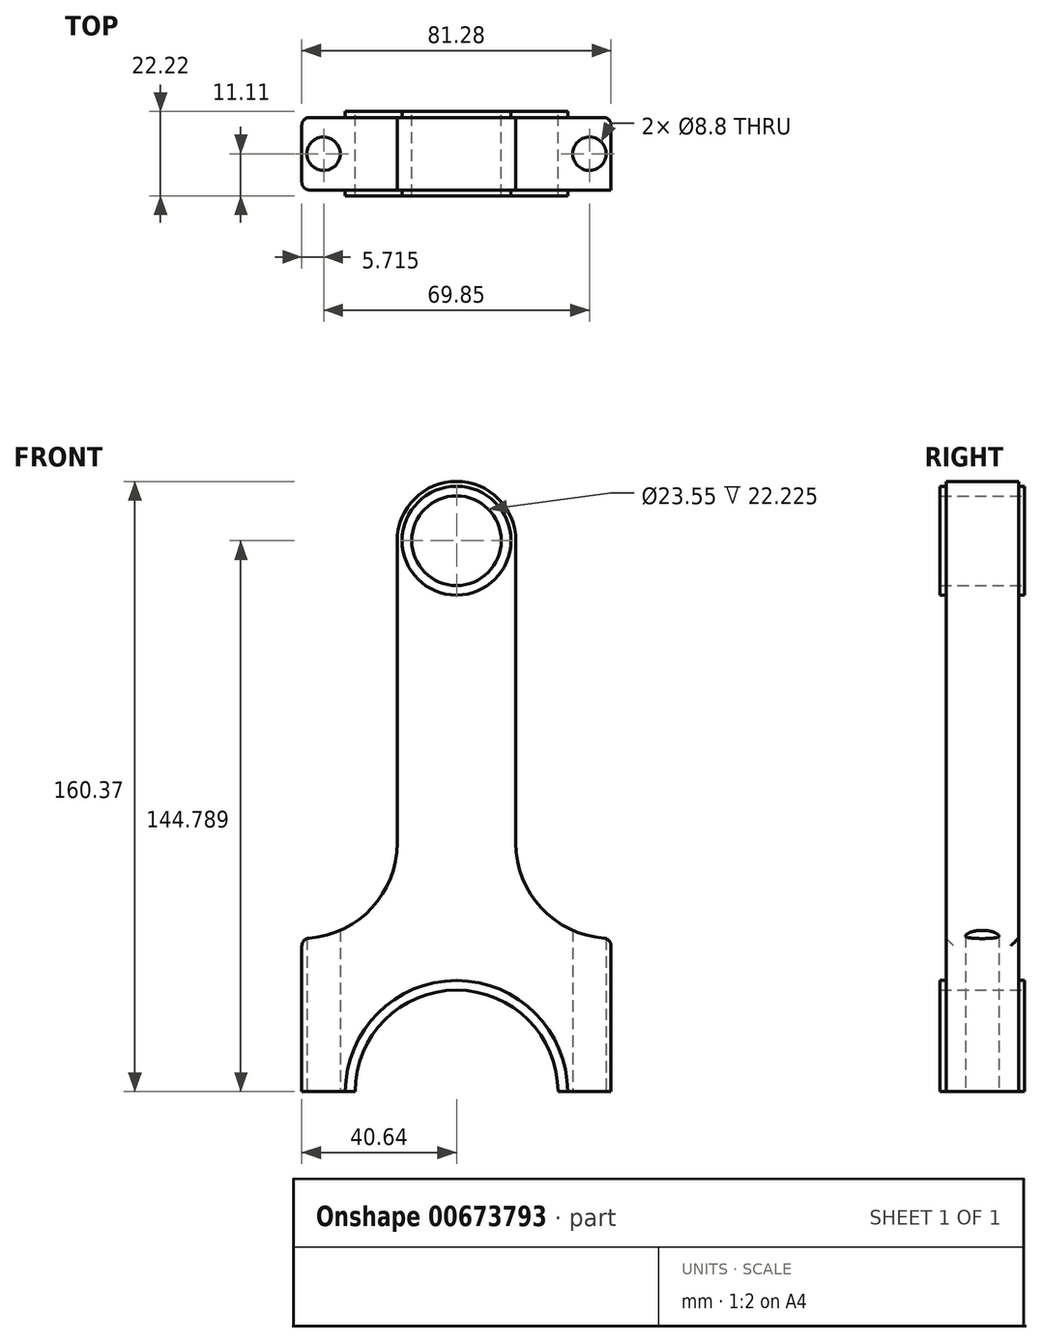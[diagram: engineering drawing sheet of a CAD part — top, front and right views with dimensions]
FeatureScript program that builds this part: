
annotation { "Feature Type Name" : "Feature", "Feature Type Description" : "" }
export const myFeature = defineFeature(function(context is Context, id is Id, definition is map)
    precondition{}
    {
        {
            var Q0;
            Q0=qCreatedBy(makeId("Front.planeOp"),FACE);
            var sketch = newSketch(context, id + "F0", { "sketchPlane" : qUnion([Q0])});
            skCircle(sketch, "E0", {"center": v(0, 0) * mm, "radius": 26.67 * mm});
            skLineSegment(sketch, "E1", {"start": v(26.67, 0) * mm, "end": v(40.64, 0) * mm});
            skLineSegment(sketch, "E2", {"start": v(40.64, 0) * mm, "end": v(40.64, 40.26) * mm});
            skArc(sketch, "E3", {"start": v(15.58, 65.32) * mm, "mid": v(22.92, 47.6) * mm, "end": v(40.64, 40.26) * mm});
            skLineSegment(sketch, "E4", {"start": v(15.58, 65.32) * mm, "end": v(15.58, 144.79) * mm});
            skLineSegment(sketch, "E5", {"start": v(40.64, 40.26) * mm, "end": v(98.37, 40.26) * mm, "construction": true});
            skCircle(sketch, "E6", {"center": v(0, 144.79) * mm, "radius": 11.77 * mm});
            skCircle(sketch, "E7", {"center": v(0, 144.79) * mm, "radius": 15.58 * mm});
            skCircle(sketch, "E8", {"center": v(0, 144.79) * mm, "radius": 14.31 * mm});
            skLineSegment(sketch, "E9.MirrorCS", {"start": v(-15.58, 65.32) * mm, "end": v(-15.58, 144.79) * mm});
            skArc(sketch, "E10.MirrorCS", {"start": v(-15.58, 65.32) * mm, "mid": v(-22.92, 47.6) * mm, "end": v(-40.64, 40.26) * mm});
            skLineSegment(sketch, "E11.MirrorCS", {"start": v(-40.64, 0) * mm, "end": v(-40.64, 40.26) * mm});
            skLineSegment(sketch, "E12.MirrorCS", {"start": v(-26.67, 0) * mm, "end": v(-40.64, 0) * mm});
            skCircle(sketch, "E13", {"center": v(0, 0) * mm, "radius": 29.21 * mm});
            skSolve(sketch);
        }
        {
            var Q0;
            {var subQ6=sQuery(id+"F0.wireOp",EDGE,"E2");Q0=makeQuery(id+"F0.imprint","IMPRINT",FACE,{"disambiguationData":[TD([[makeQuery(id+"F0.imprint","IMPRINT",EDGE,{"derivedFrom":subQ6}),1.0]])]});}
            var Q1;
            Q1=makeQuery(id+"F0.imprint","IMPRINT",FACE,{"disambiguationData":[TD([[makeQuery(id+"F0.imprint","IMPRINT",EDGE,{"derivedFrom":sQuery(id+"F0.wireOp",EDGE,"E8")}),-1.0]])]});
            extrude(context, id + "F1", {"entities" : qUnion([Q0, Q1]), "depth" : 19.05 * mm, "offsetDistance" : 25 * mm, "symmetric" : true});
        }
        {
            var Q0;
            {var subQ0=sQuery(id+"F0.wireOp",EDGE,"E1");var subQ1=sQuery(id+"F0.wireOp",EDGE,"E0");var subQ2=makeQuery(id+"F0.imprint","INTERSECT",VERTEX,{"derivedFrom":[subQ1,subQ0]});Q0=makeQuery(id+"F0.imprint","IMPRINT",FACE,{"disambiguationData":[TD([[makeQuery(id+"F0.imprint","IMPRINT",EDGE,{"disambiguationData":[TD([[subQ2,-1.0]])],"derivedFrom":subQ1}),-1.0]])]});}
            var Q1;
            Q1=makeQuery(id+"F0.imprint","IMPRINT",FACE,{"disambiguationData":[TD([[makeQuery(id+"F0.imprint","IMPRINT",EDGE,{"derivedFrom":sQuery(id+"F0.wireOp",EDGE,"E6")}),-1.0]])]});
            extrude(context, id + "F2", {"entities" : qUnion([Q0, Q1]), "operationType" : NewBodyOperationType.ADD, "depth" : 22.23 * mm, "offsetDistance" : 25 * mm, "symmetric" : true});
        }
        {
            var Q0;
            Q0=makeQuery(id+"F1.opExtrude","CAP_EDGE",EDGE,{"disambiguationData":[OSD([sQuery(id+"F0.wireOp",EDGE,"E13")])],"isStart":false});
            var Q1;
            Q1=makeQuery(id+"F1.opExtrude","CAP_EDGE",EDGE,{"disambiguationData":[OSD([sQuery(id+"F0.wireOp",EDGE,"E13")])],"isStart":true});
            var Q2;
            Q2=makeQuery(id+"F1.opExtrude","CAP_EDGE",EDGE,{"disambiguationData":[OSD([sQuery(id+"F0.wireOp",EDGE,"E11.MirrorCS")])],"isStart":true});
            var Q3;
            Q3=makeQuery(id+"F1.opExtrude","SWEPT_EDGE",EDGE,{"disambiguationData":[OSD([sQuery(id+"F0.wireOp",EDGE,"E10.MirrorCS"),sQuery(id+"F0.wireOp",EDGE,"E11.MirrorCS")])]});
            var Q4;
            Q4=makeQuery(id+"F1.opExtrude","CAP_EDGE",EDGE,{"disambiguationData":[OSD([sQuery(id+"F0.wireOp",EDGE,"E11.MirrorCS")])],"isStart":false});
            var Q5;
            Q5=makeQuery(id+"F1.opExtrude","CAP_EDGE",EDGE,{"disambiguationData":[OSD([sQuery(id+"F0.wireOp",EDGE,"E2")])],"isStart":true});
            var Q6;
            Q6=makeQuery(id+"F1.opExtrude","SWEPT_EDGE",EDGE,{"disambiguationData":[OSD([sQuery(id+"F0.wireOp",EDGE,"E2"),sQuery(id+"F0.wireOp",EDGE,"E3")])]});
            var Q7;
            Q7=makeQuery(id+"F1.opExtrude","CAP_EDGE",EDGE,{"disambiguationData":[OSD([sQuery(id+"F0.wireOp",EDGE,"E8")])],"isStart":true});
            var Q8;
            Q8=makeQuery(id+"F1.opExtrude","CAP_EDGE",EDGE,{"disambiguationData":[OSD([sQuery(id+"F0.wireOp",EDGE,"E8")])],"isStart":false});
            fillet(context, id + "F3", {"entities" : qUnion([Q0, Q1, Q2, Q3, Q4, Q5, Q6, Q7, Q8]), "radius" : 2 * mm, "tangentPropagation" : true, "allowEdgeOverflow" : false});
        }
        {
            var Q0;
            Q0=qCreatedBy(makeId("Top.planeOp"),FACE);
            var sketch = newSketch(context, id + "F4", { "sketchPlane" : qUnion([Q0])});
            skLineSegment(sketch, "E14.0", {"start": v(-40.64, -7.53) * mm, "end": v(-40.64, 7.52) * mm, "construction": true});
            skPoint(sketch, "E15.0", {"position": v(-29.21, -11.11) * mm});
            skPoint(sketch, "E16.0", {"position": v(-29.21, 11.11) * mm});
            skLineSegment(sketch, "E17", {"start": v(-29.21, 11.11) * mm, "end": v(-29.21, -11.11) * mm, "construction": true});
            skLineSegment(sketch, "E18", {"start": v(-40.64, 0) * mm, "end": v(-29.21, 0) * mm, "construction": true});
            skPoint(sketch, "E19", {"position": v(-34.92, 0) * mm});
            skPoint(sketch, "E20.MirrorP", {"position": v(34.92, 0) * mm});
            skSolve(sketch);
        }
        {
            var Q0;
            Q0=sQuery(id+"F4.wireOp",VERTEX,"E19");
            var Q1;
            Q1=sQuery(id+"F4.wireOp",VERTEX,"E20.MirrorP");
            var Q2;
            Q2=makeQuery(id+"F1.opExtrude","SWEPT_BODY",BODY,{"disambiguationData":[OSD([sQuery(id+"F0.wireOp",EDGE,"E1"),sQuery(id+"F0.wireOp",EDGE,"E2"),sQuery(id+"F0.wireOp",EDGE,"E3"),sQuery(id+"F0.wireOp",EDGE,"E4"),sQuery(id+"F0.wireOp",EDGE,"E7"),sQuery(id+"F0.wireOp",EDGE,"E8"),sQuery(id+"F0.wireOp",EDGE,"E9.MirrorCS"),sQuery(id+"F0.wireOp",EDGE,"E10.MirrorCS"),sQuery(id+"F0.wireOp",EDGE,"E11.MirrorCS"),sQuery(id+"F0.wireOp",EDGE,"E12.MirrorCS"),sQuery(id+"F0.wireOp",EDGE,"E13")])]});
            hole(context, id + "F5", {"style" : HoleStyle.SIMPLE, "endStyle" : HoleEndStyle.THROUGH, "oppositeDirection" : true, "standardTappedOrClearance" : lookupTablePath({ "standard" : "ISO", "fit" : "Normal", "size" : "M8", "type" : "Clearance" }), "standardBlindInLast" : lookupTablePath({ "fit" : "Standard", "standard" : "ISO", "size" : "M8", "type" : "Clearance" }), "holeDiameter" : 8.8 * mm, "majorDiameter" : 5 * mm, "isTappedThrough" : true, "tappedDepth" : 12 * mm, "tapClearance" : 3, "startFromSketch" : true, "locations" : qUnion([Q0, Q1]), "scope" : qUnion([Q2])});
        }
    });
